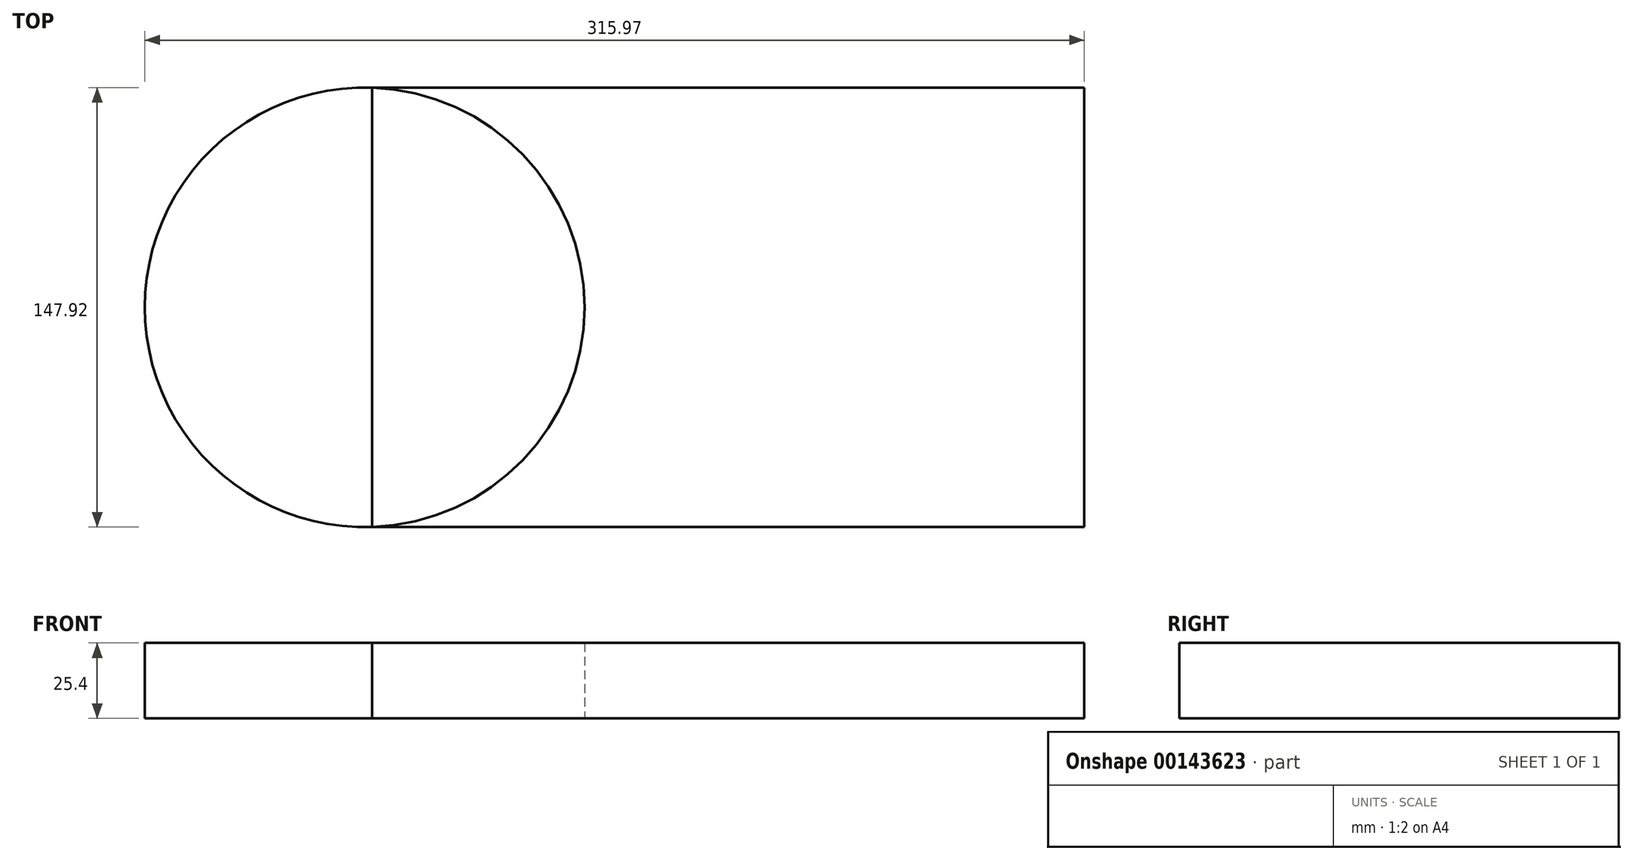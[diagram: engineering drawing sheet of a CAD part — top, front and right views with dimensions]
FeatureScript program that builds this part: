
annotation { "Feature Type Name" : "Feature", "Feature Type Description" : "" }
export const myFeature = defineFeature(function(context is Context, id is Id, definition is map)
    precondition{}
    {
        {
            var Q0;
            Q0=qCreatedBy(makeId("Top.planeOp"),FACE);
            var sketch = newSketch(context, id + "F0", { "sketchPlane" : qUnion([Q0])});
            skLineSegment(sketch, "E0.bottom", {"start": v(119.76, 73.96) * mm, "end": v(-119.76, 73.96) * mm});
            skLineSegment(sketch, "E0.top", {"start": v(119.76, -73.96) * mm, "end": v(-119.76, -73.96) * mm});
            skLineSegment(sketch, "E0.left", {"start": v(119.76, 73.96) * mm, "end": v(119.76, -73.96) * mm});
            skLineSegment(sketch, "E0.right", {"start": v(-119.76, 73.96) * mm, "end": v(-119.76, -73.96) * mm});
            skPoint(sketch, "E0.middle", {"position": v(0, 0) * mm});
            skSolve(sketch);
        }
        {
            var Q0;
            Q0=makeQuery(id+"F0.imprint","IMPRINT",FACE,{"disambiguationData":[TD([[makeQuery(id+"F0.imprint","IMPRINT",EDGE,{"derivedFrom":sQuery(id+"F0.wireOp",EDGE,"E0.bottom")}),1.0]])]});
            var sketch = newSketch(context, id + "F1", { "sketchPlane" : qUnion([Q0])});
            skCircle(sketch, "E1", {"center": v(-122.26, 0) * mm, "radius": 73.96 * mm});
            skSolve(sketch);
        }
        {
            var Q0;
            {var subQ0=makeQuery(id+"F0.imprint","IMPRINT",EDGE,{"derivedFrom":sQuery(id+"F0.wireOp",EDGE,"E0.bottom")});Q0=makeQuery(id+"F1.imprint","IMPRINT",FACE,{"disambiguationData":[TD([[makeQuery(id+"F1.imprint","IMPRINT",EDGE,{"derivedFrom":subQ0}),1.0]])]});}
            var Q1;
            Q1=makeQuery(id+"F0.imprint","IMPRINT",FACE,{"disambiguationData":[TD([[makeQuery(id+"F0.imprint","IMPRINT",EDGE,{"derivedFrom":sQuery(id+"F0.wireOp",EDGE,"E0.bottom")}),1.0]])]});
            var Q2;
            {var subQ0=sQuery(id+"F1.wireOp",EDGE,"E1");var subQ1=makeQuery(id+"F0.imprint","IMPRINT",EDGE,{"derivedFrom":sQuery(id+"F0.wireOp",EDGE,"E0.right")});var subQ2=makeQuery(id+"F1.imprint","INTERSECT",VERTEX,{"disambiguationData":[OD(0.0)],"derivedFrom":[subQ1,subQ0]});Q2=makeQuery(id+"F1.imprint","IMPRINT",FACE,{"disambiguationData":[TD([[makeQuery(id+"F1.imprint","IMPRINT",EDGE,{"disambiguationData":[TD([[subQ2,-1.0]])],"derivedFrom":subQ0}),1.0]])]});}
            extrude(context, id + "F3", {"entities" : qUnion([Q0, Q1, Q2]), "depth" : 25.4 * mm});
        }
    });
